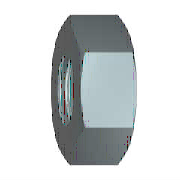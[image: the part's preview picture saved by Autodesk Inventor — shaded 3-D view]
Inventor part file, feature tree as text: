
AUTODESK INVENTOR PART (.ipt)
format: ipt  version: 2020 (Build 240168000, 168)  size: 167,424 bytes
history: native  units: mm (DEFAULTED — no unit token found)
features: sketch x3, other x2, extrude x1, hole x1, plane x1
ambient origin geometry x7: Origin, YZ Plane, XZ Plane, X Axis, Y Axis, Z Axis, Center Point
bodies: Solid1 (feature_tree)
feature tree (8):
  extrude  "Bryła"  Depth=11.547005mm
  other  "Faza1"
  hole  "Gwint"  [1 undecoded]
  other  "Work Axis1"
  plane  "Work Plane1"
  sketch  "Szkic1"
  sketch  "Szkic2"
  sketch  "Szkic3"
note: 1 required parameter value undecoded (feature->parameter linkage not recoverable at this tier; creation-order binding heuristic only, values carry confidence <= 0.55)
